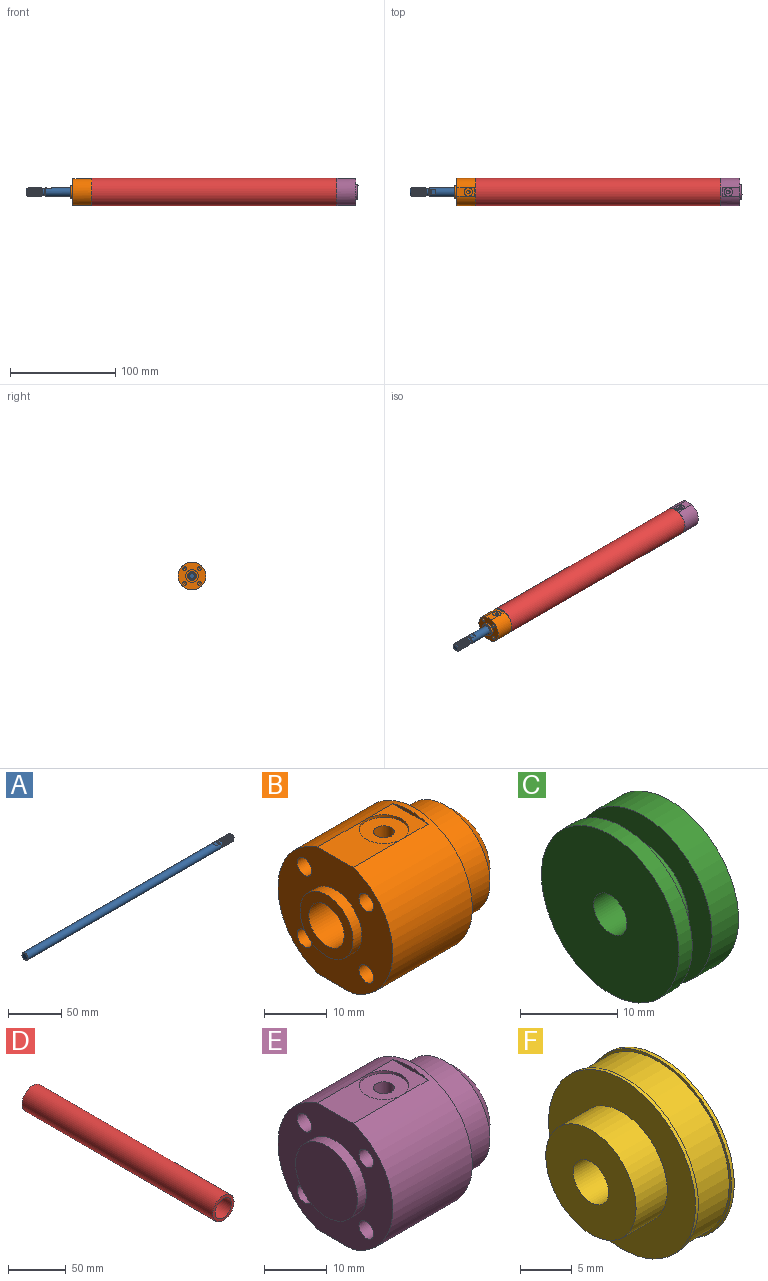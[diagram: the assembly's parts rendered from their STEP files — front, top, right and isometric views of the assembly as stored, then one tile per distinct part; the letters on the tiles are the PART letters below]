
ASSEMBLY  parts=6 mates=5
PART A: 19 faces, bbox 276.4x8x9.2 mm
  f0: plane 7x7mm, normal (-1,0,0), area 5.3mm2, adj f4,f16
  f1: cylinder r=4mm len=257.43mm, axis (1,0,0), area 6442.4mm2, adj f7,f8,f9,f14,f15,f17,f18
  f2: plane 5x5mm, normal (1,0,0), area 19.6mm2, adj f13
  f3: cylinder r=4mm len=13.5mm, axis (1,0,0), area 2.5mm2, adj f10,f11,f12,f13,f16
  f4: cylinder r=3.25mm len=6.5mm, axis (1,0,0), area 51.1mm2, adj f0,f5
  f5: plane 7x7mm, normal (1,0,0), area 5.3mm2, adj f4,f17
  f6: plane 7x7mm, normal (-1,0,0), area 38.5mm2, adj f18
  f7: plane 5.29x0mm, normal (1,0,0), area 0mm2, adj f1,f9,f15
  f8: plane 5.29x0mm, normal (-1,0,0), area 0mm2, adj f1,f9,f14
  f9: plane 5.29x4mm, normal (0,0,1), area 21.2mm2, adj f1,f7,f8
  f10: bspline ~15.12x9.24mm, area 281.9mm2, adj f3,f11,f12,f13
  f11: plane 0.78x0.63mm, normal (0,0,-1), area 0.2mm2, adj f3,f10,f12,f16
  f12: bspline ~15.12x9.24mm, area 289.3mm2, adj f3,f10,f11,f13,f16
  f13: cone r=2.5mm half-angle=45deg, axis (-1,0,0), area 31.7mm2, adj f2,f3,f10,f12
  f14: plane 5.28x1mm, normal (-0.87,0,0.5), area 4.2mm2, adj f1,f8
  f15: plane 5.28x1mm, normal (0.87,0,0.5), area 4.2mm2, adj f1,f7
  f16: cone r=4mm half-angle=45deg, axis (1,0,0), area 10.6mm2, adj f0,f3,f11,f12
  f17: cone r=3.5mm half-angle=45deg, axis (-1,0,0), area 16.7mm2, adj f1,f5
  f18: cone r=4mm half-angle=45deg, axis (1,0,0), area 16.7mm2, adj f1,f6
PART B: 32 faces, bbox 29.5x26x26 mm
  f0: plane 11x8mm, normal (0,0,1), area 62.9mm2, adj f1,f2,f24
  f1: cylinder r=13mm len=26mm, axis (1,0,0), area 1193.7mm2, adj f0,f2,f5,f20,f21,f22,f23,f28
  f2: plane 26x24.74mm, normal (-1,0,0), area 376.9mm2, adj f0,f1,f6,f8,f10,f12,f14,f20
  f3: plane 10x10mm, normal (1,0,0), area 28.3mm2, adj f4,f16
  f4: cylinder r=4mm len=20mm, axis (1,0,0), area 502.7mm2, adj f3,f7
  f5: plane 26x26mm, normal (1,0,0), area 216.8mm2, adj f1,f17
  f6: cylinder r=6mm len=12mm, axis (1,0,0), area 75.4mm2, adj f2,f7
  f7: plane 12x12mm, normal (-1,0,0), area 62.8mm2, adj f4,f6
  f8: cylinder r=1.65mm len=7mm, axis (-1,0,0), area 72.6mm2, adj f2,f9
  f9: cone r=0mm half-angle=59deg, axis (-1,0,0), area 10mm2, adj f8
  f10: cylinder r=1.65mm len=7mm, axis (-1,0,0), area 72.6mm2, adj f2,f11
  f11: cone r=0mm half-angle=59deg, axis (-1,0,0), area 10mm2, adj f10
  f12: cylinder r=1.65mm len=7mm, axis (-1,0,0), area 72.6mm2, adj f2,f13
  f13: cone r=0mm half-angle=59deg, axis (-1,0,0), area 10mm2, adj f12
  f14: cylinder r=1.65mm len=7mm, axis (-1,0,0), area 72.6mm2, adj f2,f15
  f15: cone r=0mm half-angle=59deg, axis (-1,0,0), area 10mm2, adj f14
  f16: cylinder r=5mm len=10mm, axis (-1,0,0), area 298.5mm2, adj f3,f18
  f17: cylinder r=10mm len=20mm, axis (-1,0,0), area 439.8mm2, adj f5,f19
  f18: plane 15x15mm, normal (1,0,0), area 98.2mm2, adj f16,f19
  f19: cone r=7.5mm half-angle=45deg, axis (-1,0,0), area 194.4mm2, adj f17,f18
  f20: plane 17x8mm, normal (0,0,-1), area 85.8mm2, adj f1,f2,f21,f28
  f21: plane 8x0.63mm, normal (-1,0,0), area 3.4mm2, adj f1,f20
  f22: plane 8x6mm, normal (0,0,1), area 22.9mm2, adj f1,f23,f24
  f23: plane 8x0.63mm, normal (-1,0,0), area 3.4mm2, adj f1,f22
  f24: cylinder r=4mm len=8mm, axis (0,0,1), area 12.6mm2, adj f0,f22,f25
  f25: plane 8x8mm, normal (0,0,1), area 41.7mm2, adj f24,f27
  f26: cone r=0mm half-angle=59deg, axis (0,0,1), area 10mm2, adj f27
  f27: cylinder r=1.65mm len=4.7mm, axis (0,0,1), area 48.7mm2, adj f25,f26
  f28: cylinder r=4mm len=8mm, axis (0,0,-1), area 12.6mm2, adj f1,f20,f29
  f29: plane 8x8mm, normal (0,0,-1), area 41.7mm2, adj f28,f31
  f30: cone r=0mm half-angle=59deg, axis (0,0,-1), area 10mm2, adj f31
  f31: cylinder r=1.65mm len=4.7mm, axis (0,0,-1), area 48.7mm2, adj f29,f30
PART C: 10 faces, bbox 8.7x20x20 mm
  f0: cylinder r=2.4mm len=4.8mm, axis (-1,0,0), area 72.4mm2, adj f1,f9
  f1: plane 12.3x12.3mm, normal (1,0,0), area 100.7mm2, adj f0,f2
  f2: cylinder r=6.15mm len=12.3mm, axis (-1,0,0), area 148.8mm2, adj f1,f3
  f3: plane 20x20mm, normal (1,0,0), area 195.3mm2, adj f2,f4
  f4: cylinder r=10mm len=20mm, axis (-1,0,0), area 241.9mm2, adj f3,f5
  f5: plane 20x20mm, normal (-1,0,0), area 175.6mm2, adj f4,f6
  f6: cylinder r=6.64mm len=13.28mm, axis (-1,0,0), area 120.2mm2, adj f5,f7
  f7: plane 20x20mm, normal (1,0,0), area 175.6mm2, adj f6,f8
  f8: cylinder r=10mm len=20mm, axis (-1,0,0), area 120.6mm2, adj f7,f9
  f9: plane 20x20mm, normal (-1,0,0), area 296.1mm2, adj f0,f8
PART D: 4 faces, bbox 26x233x26 mm
  f0: cylinder r=10mm len=233mm, axis (0,1,0), area 14639.8mm2, adj f2,f3
  f1: cylinder r=13mm len=233mm, axis (0,1,0), area 19031.8mm2, adj f2,f3
  f2: plane 26x26mm, normal (0,-1,0), area 216.8mm2, adj f0,f1
  f3: plane 26x26mm, normal (0,1,0), area 216.8mm2, adj f0,f1
PART E: 31 faces, bbox 29.5x26x26 mm
  f0: cylinder r=10mm len=20mm, axis (-1,0,0), area 439.8mm2, adj f4,f30
  f1: plane 11x8mm, normal (0,0,1), area 62.9mm2, adj f2,f3,f19
  f2: cylinder r=13mm len=26mm, axis (1,0,0), area 1193.7mm2, adj f1,f3,f4,f15,f16,f17,f18,f23
  f3: plane 26x24.74mm, normal (-1,0,0), area 336mm2, adj f1,f2,f5,f7,f9,f11,f13,f15
  f4: plane 26x26mm, normal (1,0,0), area 216.8mm2, adj f0,f2
  f5: cylinder r=7mm len=14mm, axis (1,0,0), area 88mm2, adj f3,f6
  f6: plane 14x14mm, normal (-1,0,0), area 153.9mm2, adj f5
  f7: cylinder r=1.65mm len=7mm, axis (-1,0,0), area 72.6mm2, adj f3,f8
  f8: cone r=0mm half-angle=59deg, axis (-1,0,0), area 10mm2, adj f7
  f9: cylinder r=1.65mm len=7mm, axis (-1,0,0), area 72.6mm2, adj f3,f10
  f10: cone r=0mm half-angle=59deg, axis (-1,0,0), area 10mm2, adj f9
  f11: cylinder r=1.65mm len=7mm, axis (-1,0,0), area 72.6mm2, adj f3,f12
  f12: cone r=0mm half-angle=59deg, axis (-1,0,0), area 10mm2, adj f11
  f13: cylinder r=1.65mm len=7mm, axis (-1,0,0), area 72.6mm2, adj f3,f14
  f14: cone r=0mm half-angle=59deg, axis (-1,0,0), area 10mm2, adj f13
  f15: plane 17x8mm, normal (0,0,-1), area 85.8mm2, adj f2,f3,f16,f23
  f16: plane 8x0.63mm, normal (-1,0,0), area 3.4mm2, adj f2,f15
  f17: plane 8x6mm, normal (0,0,1), area 22.9mm2, adj f2,f18,f19
  f18: plane 8x0.63mm, normal (-1,0,0), area 3.4mm2, adj f2,f17
  f19: cylinder r=4mm len=8mm, axis (0,0,1), area 12.6mm2, adj f1,f17,f20
  f20: plane 8x8mm, normal (0,0,1), area 41.7mm2, adj f19,f22
  f21: cone r=0mm half-angle=59deg, axis (0,0,1), area 10mm2, adj f22
  f22: cylinder r=1.65mm len=4.7mm, axis (0,0,1), area 48.7mm2, adj f20,f21
  f23: cylinder r=4mm len=8mm, axis (0,0,-1), area 12.6mm2, adj f2,f15,f24
  f24: plane 8x8mm, normal (0,0,-1), area 41.7mm2, adj f23,f26
  f25: cone r=0mm half-angle=59deg, axis (0,0,-1), area 10mm2, adj f26
  f26: cylinder r=1.65mm len=4.7mm, axis (0,0,-1), area 48.7mm2, adj f24,f25
  f27: plane 15x15mm, normal (1,0,0), area 98.2mm2, adj f29,f30
  f28: plane 10x10mm, normal (1,0,0), area 78.5mm2, adj f29
  f29: cylinder r=5mm len=10mm, axis (1,0,0), area 298.5mm2, adj f27,f28
  f30: cone r=7.5mm half-angle=45deg, axis (-1,0,0), area 194.4mm2, adj f0,f27
PART F: 12 faces, bbox 9.5x20x20 mm
  f0: cylinder r=9.7mm len=19.4mm, axis (-1,0,0), area 274.3mm2, adj f1,f11
  f1: plane 20x20mm, normal (1,0,0), area 18.6mm2, adj f0,f2
  f2: cylinder r=10mm len=20mm, axis (-1,0,0), area 24.5mm2, adj f1,f3
  f3: plane 20x20mm, normal (-1,0,0), area 195.3mm2, adj f2,f4
  f4: cylinder r=6.15mm len=12.3mm, axis (-1,0,0), area 163.6mm2, adj f3,f5
  f5: plane 12.3x12.3mm, normal (-1,0,0), area 100.7mm2, adj f4,f6
  f6: cylinder r=2.4mm len=5.19mm, axis (-1,0,0), area 78.3mm2, adj f5,f7
  f7: plane 10x10mm, normal (1,0,0), area 60.4mm2, adj f6,f8
  f8: cylinder r=5mm len=10mm, axis (-1,0,0), area 135.7mm2, adj f7,f9
  f9: plane 20x20mm, normal (1,0,0), area 235.6mm2, adj f8,f10
  f10: cylinder r=10mm len=20mm, axis (-1,0,0), area 24.5mm2, adj f9,f11
  f11: plane 20x20mm, normal (-1,0,0), area 18.6mm2, adj f0,f10
PLACE A rot(axis=(0,0,-1),180deg) t=(883.79,-212.5,235.29)mm
PLACE B rot(axis=(0.98,0.2,0.06),0deg) t=(669.9,-212.5,235.29)mm
PLACE C rot(axis=(0,-1,0),180deg) t=(888.4,-212.5,235.29)mm
PLACE D rot(axis=(0,0,1),90deg) t=(669.9,-212.5,235.29)mm
PLACE E rot(axis=(0,-1,0),180deg) t=(902.9,-212.5,235.29)mm
PLACE F rot(axis=(0,-1,0),180deg) t=(888.98,-212.5,235.29)mm
MATE slider D.f0 <-> C.f0  axis (-1,0,0) through (902.9,-212.5,235.29)mm
MATE fastened D.f0 <-> E.f2  axis (1,0,0) through (902.9,-212.5,235.29)mm
MATE fastened F.f0 <-> A.f1  axis (1,0,0) through (883.79,-212.5,235.29)mm
MATE fastened C.f0 <-> F.f0  axis (-1,0,0) through (884.75,-212.5,235.29)mm
MATE fastened B.f16 <-> D.f0  axis (-1,0,0) through (669.9,-212.5,235.29)mm
